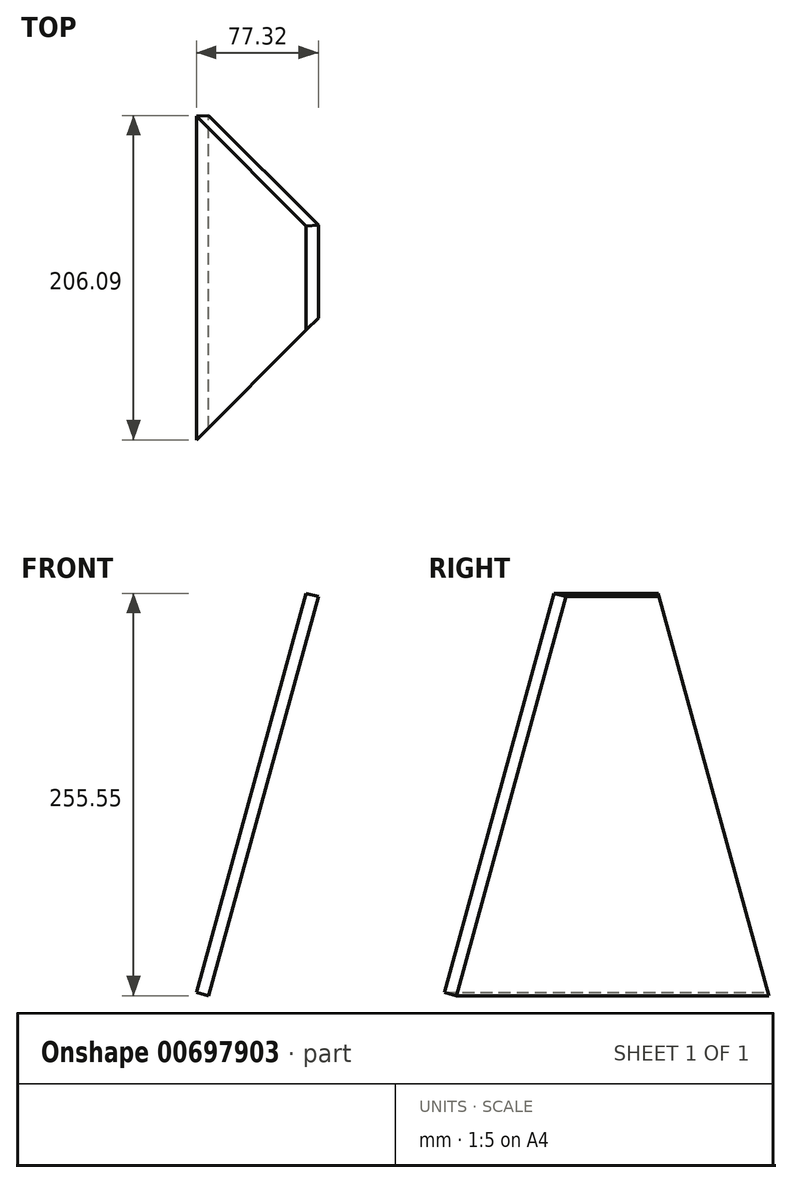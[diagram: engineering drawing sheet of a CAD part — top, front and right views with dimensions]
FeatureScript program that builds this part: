
annotation { "Feature Type Name" : "Feature", "Feature Type Description" : "" }
export const myFeature = defineFeature(function(context is Context, id is Id, definition is map)
    precondition{}
    {
        {
            var Q0;
            Q0=qCreatedBy(makeId("Front.planeOp"),FACE);
            var sketch = newSketch(context, id + "F0", { "sketchPlane" : qUnion([Q0])});
            skLineSegment(sketch, "E0", {"start": v(0, 212.24) * mm, "end": v(0, -177.02) * mm, "construction": true});
            skLineSegment(sketch, "E1", {"start": v(0, -177.02) * mm, "end": v(106.9, -177.02) * mm, "construction": true});
            skLineSegment(sketch, "E2", {"start": v(0, 212.24) * mm, "end": v(106.9, -177.02) * mm, "construction": true});
            skLineSegment(sketch, "E3.MirrorCS", {"start": v(0, 212.24) * mm, "end": v(-106.9, -177.02) * mm, "construction": true});
            skLineSegment(sketch, "E4.MirrorCS", {"start": v(0, -177.02) * mm, "end": v(-106.9, -177.02) * mm, "construction": true});
            skLineSegment(sketch, "E5", {"start": v(0, -177.02) * mm, "end": v(0, 76.42) * mm, "construction": true});
            skLineSegment(sketch, "E6", {"start": v(0, 76.42) * mm, "end": v(37.3, 76.42) * mm, "construction": true});
            skCircle(sketch, "E7", {"center": v(106.9, -177.02) * mm, "radius": 8 * mm, "construction": true});
            skCircle(sketch, "E8", {"center": v(37.3, 76.42) * mm, "radius": 8 * mm, "construction": true});
            skLineSegment(sketch, "E9", {"start": v(37.3, 76.42) * mm, "end": v(-126.4, 31.47) * mm, "construction": true});
            skLineSegment(sketch, "E10", {"start": v(29.58, 74.3) * mm, "end": v(99.19, -179.13) * mm});
            skLineSegment(sketch, "E11", {"start": v(99.19, -179.13) * mm, "end": v(106.9, -177.02) * mm});
            skLineSegment(sketch, "E12", {"start": v(29.58, 74.3) * mm, "end": v(37.3, 76.42) * mm});
            skLineSegment(sketch, "E13", {"start": v(37.3, 76.42) * mm, "end": v(106.9, -177.02) * mm});
            skSolve(sketch);
        }
        {
            var Q0;
            Q0=makeQuery(id+"F0.imprint","IMPRINT",FACE,{"disambiguationData":[TD([[makeQuery(id+"F0.imprint","IMPRINT",EDGE,{"derivedFrom":sQuery(id+"F0.wireOp",EDGE,"E10")}),1.0]])]});
            extrude(context, id + "F1", {"entities" : qUnion([Q0]), "depth" : 120 * mm, "offsetDistance" : 25 * mm, "hasSecondDirection" : true, "secondDirectionOppositeDirection" : true, "secondDirectionDepth" : 120 * mm});
        }
        {
            var Q0;
            Q0=makeQuery(id+"F1.opExtrude","SWEPT_BODY",BODY,{"disambiguationData":[OSD([sQuery(id+"F0.wireOp",EDGE,"E10"),sQuery(id+"F0.wireOp",EDGE,"E11"),sQuery(id+"F0.wireOp",EDGE,"E12"),sQuery(id+"F0.wireOp",EDGE,"E13")])]});
            var Q1;
            Q1=qCreatedBy(makeId("Right.planeOp"),FACE);
            mirror(context, id + "F2", {"entities" : qUnion([Q0]), "mirrorPlane" : qUnion([Q1])});
        }
        {
            var Q0;
            Q0=qCreatedBy(makeId("Front.planeOp"),FACE);
            var sketch = newSketch(context, id + "F3", { "sketchPlane" : qUnion([Q0])});
            skLineSegment(sketch, "E14", {"start": v(0, 0) * mm, "end": v(0, 76.6) * mm});
            skSolve(sketch);
        }
        {
            var Q0;
            Q0=makeQuery(id+"F1.opExtrude","SWEPT_BODY",BODY,{"disambiguationData":[OSD([sQuery(id+"F0.wireOp",EDGE,"E10"),sQuery(id+"F0.wireOp",EDGE,"E11"),sQuery(id+"F0.wireOp",EDGE,"E12"),sQuery(id+"F0.wireOp",EDGE,"E13")])]});
            var Q1;
            Q1=sQuery(id+"F3.wireOp",EDGE,"E14");
            circularPattern(context, id + "F4", {"entities" : qUnion([Q0]), "axis" : qUnion([Q1]), "angle" : 6.28 * radian, "instanceCount" : 4, "equalSpace" : true});
        }
        {
            var Q0;
            Q0=qCreatedBy(makeId("Top.planeOp"),FACE);
            var sketch = newSketch(context, id + "F5", { "sketchPlane" : qUnion([Q0])});
            skPoint(sketch, "E15.middle", {"position": v(0, 0) * mm});
            skLineSegment(sketch, "E16.bottom", {"start": v(178.78, -178.78) * mm, "end": v(-178.78, -178.78) * mm});
            skLineSegment(sketch, "E16.left", {"start": v(178.78, -178.78) * mm, "end": v(178.78, 178.78) * mm});
            skLineSegment(sketch, "E17", {"start": v(-178.78, -178.78) * mm, "end": v(178.78, 178.78) * mm});
            skSolve(sketch);
        }
        {
            var Q0;
            Q0=makeQuery(id+"F5.imprint","IMPRINT",FACE,{"disambiguationData":[TD([[makeQuery(id+"F5.imprint","IMPRINT",EDGE,{"derivedFrom":sQuery(id+"F5.wireOp",EDGE,"E15.bottom")}),-1.0]])]});
            var Q1;
            Q1=makeQuery(id+"F5.imprint","IMPRINT",FACE,{"disambiguationData":[TD([[makeQuery(id+"F5.imprint","IMPRINT",EDGE,{"derivedFrom":sQuery(id+"F5.wireOp",EDGE,"E16.bottom")}),-1.0]])]});
            extrude(context, id + "F6", {"entities" : qUnion([Q0, Q1]), "operationType" : NewBodyOperationType.REMOVE, "oppositeDirection" : true, "depth" : 184 * mm, "offsetDistance" : 25 * mm, "hasSecondDirection" : true, "secondDirectionOppositeDirection" : false, "secondDirectionDepth" : 95 * mm});
        }
        {
            var Q0;
            Q0=makeQuery(id+"F4.opPattern","COPY",BODY,{"derivedFrom":makeQuery(id+"F1.opExtrude","SWEPT_BODY",BODY,{"disambiguationData":[OSD([sQuery(id+"F0.wireOp",EDGE,"E10"),sQuery(id+"F0.wireOp",EDGE,"E11"),sQuery(id+"F0.wireOp",EDGE,"E12"),sQuery(id+"F0.wireOp",EDGE,"E13")])]}),"instanceName":"3"});
            deleteBodies(context, id + "F7", {"entities" : qUnion([Q0])});
        }
        {
            var Q0;
            Q0=makeQuery(id+"F4.opPattern","COPY",FACE,{"derivedFrom":makeQuery(id+"F1.opExtrude","SWEPT_FACE",FACE,{"disambiguationData":[OSD([sQuery(id+"F0.wireOp",EDGE,"E10")])]}),"instanceName":"1"});
            var sketch = newSketch(context, id + "F8", { "sketchPlane" : qUnion([Q0])});
            skLineSegment(sketch, "E18.bottom", {"start": v(-265.15, 108.91) * mm, "end": v(291.54, 108.91) * mm});
            skLineSegment(sketch, "E18.top", {"start": v(-265.15, -268.89) * mm, "end": v(291.54, -268.89) * mm});
            skLineSegment(sketch, "E18.left", {"start": v(-265.15, 108.91) * mm, "end": v(-265.15, -268.89) * mm});
            skLineSegment(sketch, "E18.right", {"start": v(291.54, 108.91) * mm, "end": v(291.54, -268.89) * mm});
            skSolve(sketch);
        }
        {
            var Q0;
            {var subQ0=sQuery(id+"F0.wireOp",EDGE,"E10");Q0=makeQuery(id+"F8.imprint","IMPRINT",FACE,{"disambiguationData":[TD([[makeQuery(id+"F8.imprint","IMPRINT",EDGE,{"derivedFrom":makeQuery(id+"F4.opPattern","COPY",EDGE,{"derivedFrom":makeQuery(id+"F1.opExtrude","CAP_EDGE",EDGE,{"disambiguationData":[OSD([subQ0])],"isStart":true}),"instanceName":"1"})}),1.0]])]});}
            var Q1;
            Q1=makeQuery(id+"F8.imprint","IMPRINT",FACE,{"disambiguationData":[TD([[makeQuery(id+"F8.imprint","IMPRINT",EDGE,{"derivedFrom":sQuery(id+"F8.wireOp",EDGE,"E18.bottom")}),-1.0]])]});
            var Q2;
            Q2=sQuery(id+"F8.wireOp",EDGE,"E18.left");
            var Q3;
            Q3=sQuery(id+"F8.wireOp",EDGE,"E18.bottom");
            var Q4;
            Q4=sQuery(id+"F8.wireOp",EDGE,"E18.right");
            var Q5;
            Q5=sQuery(id+"F8.wireOp",EDGE,"E18.top");
            extrude(context, id + "F9", {"entities" : qUnion([Q0, Q1]), "operationType" : NewBodyOperationType.REMOVE, "surfaceEntities" : qUnion([Q2, Q3, Q4, Q5]), "oppositeDirection" : true, "depth" : 221 * mm, "offsetDistance" : 25 * mm});
        }
    });
